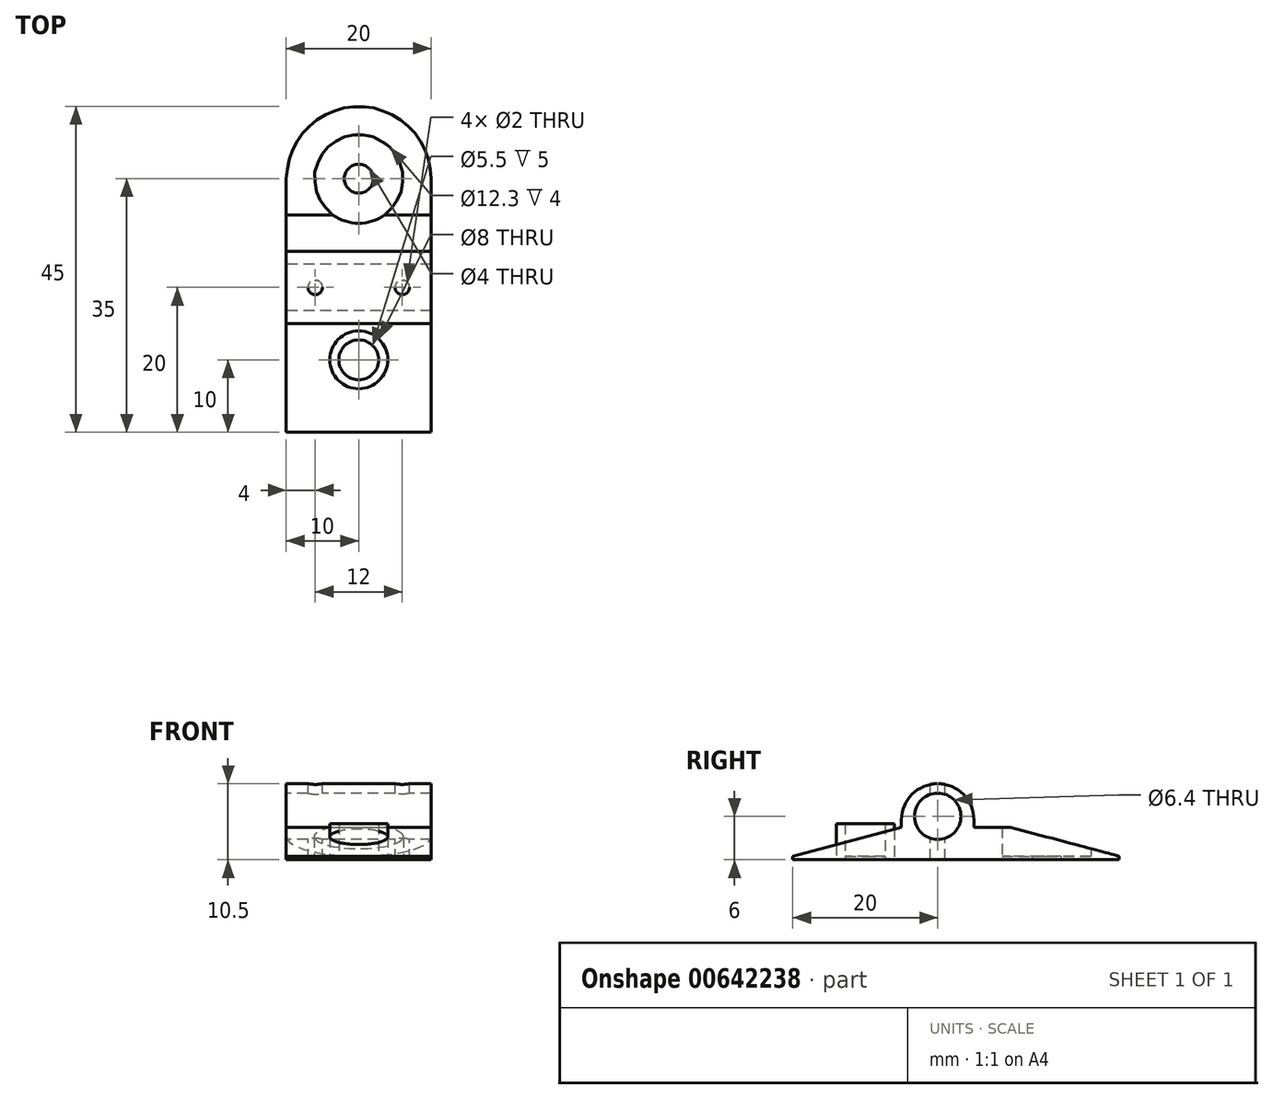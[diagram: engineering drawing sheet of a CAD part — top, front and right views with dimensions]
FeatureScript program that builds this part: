
annotation { "Feature Type Name" : "Feature", "Feature Type Description" : "" }
export const myFeature = defineFeature(function(context is Context, id is Id, definition is map)
    precondition{}
    {
        {
            var Q0;
            Q0=qCreatedBy(makeId("Top.planeOp"),FACE);
            var sketch = newSketch(context, id + "F0", { "sketchPlane" : qUnion([Q0])});
            skLineSegment(sketch, "E0.bottom", {"start": v(0, 0) * mm, "end": v(20, 0) * mm});
            skLineSegment(sketch, "E0.top", {"start": v(0, 45) * mm, "end": v(20, 45) * mm});
            skLineSegment(sketch, "E0.left", {"start": v(0, 0) * mm, "end": v(0, 45) * mm});
            skLineSegment(sketch, "E0.right", {"start": v(20, 0) * mm, "end": v(20, 45) * mm});
            skCircle(sketch, "E1", {"center": v(10, 35) * mm, "radius": 6.15 * mm});
            skCircle(sketch, "E2", {"center": v(10, 10) * mm, "radius": 2.75 * mm});
            skCircle(sketch, "E3", {"center": v(10, 35) * mm, "radius": 2 * mm});
            skCircle(sketch, "E4", {"center": v(10, 10) * mm, "radius": 4 * mm});
            skSolve(sketch);
        }
        {
            var Q0;
            Q0=makeQuery(id+"F0.imprint","IMPRINT",FACE,{"disambiguationData":[TD([[makeQuery(id+"F0.imprint","IMPRINT",EDGE,{"derivedFrom":sQuery(id+"F0.wireOp",EDGE,"E0.bottom")}),1.0]])]});
            extrude(context, id + "F1", {"entities" : qUnion([Q0]), "depth" : 4 * mm, "offsetDistance" : 25 * mm});
        }
        {
            var Q0;
            Q0=makeQuery(id+"F1.opExtrude","CAP_FACE",FACE,{"disambiguationData":[OSD([sQuery(id+"F0.wireOp",EDGE,"E0.bottom"),sQuery(id+"F0.wireOp",EDGE,"E0.top"),sQuery(id+"F0.wireOp",EDGE,"E0.left"),sQuery(id+"F0.wireOp",EDGE,"E0.right"),sQuery(id+"F0.wireOp",EDGE,"E1")])],"isStart":false});
            var Q1;
            Q1=makeQuery(id+"F0.imprint","IMPRINT",FACE,{"disambiguationData":[TD([[makeQuery(id+"F0.imprint","IMPRINT",EDGE,{"derivedFrom":sQuery(id+"F0.wireOp",EDGE,"E1")}),1.0]])]});
            var Q2;
            Q2=makeQuery(id+"F0.imprint","IMPRINT",FACE,{"disambiguationData":[TD([[makeQuery(id+"F0.imprint","IMPRINT",EDGE,{"derivedFrom":sQuery(id+"F0.wireOp",EDGE,"E2")}),1.0]])]});
            extrude(context, id + "F2", {"entities" : qUnion([Q0, Q1, Q2]), "operationType" : NewBodyOperationType.ADD, "depth" : 0.5 * mm, "offsetDistance" : 25 * mm});
        }
        {
            var Q0;
            Q0=makeQuery(id+"F2.opExtrude","CAP_FACE",FACE,{"disambiguationData":[OSD([sQuery(id+"F0.wireOp",EDGE,"E0.bottom"),sQuery(id+"F0.wireOp",EDGE,"E0.top"),sQuery(id+"F0.wireOp",EDGE,"E0.left"),sQuery(id+"F0.wireOp",EDGE,"E0.right"),sQuery(id+"F0.wireOp",EDGE,"E1")])],"isStart":false});
            var sketch = newSketch(context, id + "F3", { "sketchPlane" : qUnion([Q0])});
            skLineSegment(sketch, "E5.bottom", {"start": v(0, 15) * mm, "end": v(20, 15) * mm});
            skLineSegment(sketch, "E5.top", {"start": v(0, 25) * mm, "end": v(20, 25) * mm});
            skLineSegment(sketch, "E5.left", {"start": v(0, 15) * mm, "end": v(0, 25) * mm});
            skLineSegment(sketch, "E5.right", {"start": v(20, 15) * mm, "end": v(20, 25) * mm});
            skSolve(sketch);
        }
        {
            var Q0;
            Q0=makeQuery(id+"F2.opExtrude","CAP_EDGE",EDGE,{"disambiguationData":[OSD([sQuery(id+"F0.wireOp",EDGE,"E0.bottom")])],"isStart":false});
            chamfer(context, id + "F4", {"entities" : qUnion([Q0]), "chamferType" : ChamferType.TWO_OFFSETS, "width1" : 15 * mm, "oppositeDirection" : false, "width2" : 4 * mm, "tangentPropagation" : true});
        }
        {
            var Q0;
            Q0=makeQuery(id+"F0.imprint","IMPRINT",FACE,{"disambiguationData":[TD([[makeQuery(id+"F0.imprint","IMPRINT",EDGE,{"derivedFrom":sQuery(id+"F0.wireOp",EDGE,"E2")}),-1.0]])]});
            extrude(context, id + "F5", {"entities" : qUnion([Q0]), "depth" : 5 * mm, "offsetDistance" : 25 * mm});
        }
        {
            var Q0;
            Q0=makeQuery(id+"F3.imprint","IMPRINT",FACE,{"disambiguationData":[TD([[makeQuery(id+"F3.imprint","IMPRINT",EDGE,{"derivedFrom":sQuery(id+"F3.wireOp",EDGE,"E5.bottom")}),1.0]])]});
            extrude(context, id + "F6", {"entities" : qUnion([Q0]), "operationType" : NewBodyOperationType.ADD, "depth" : 6 * mm, "offsetDistance" : 25 * mm});
        }
        {
            var Q0;
            {var subQ0=sQuery(id+"F0.wireOp",EDGE,"E0.left");Q0=makeQuery(id+"F6.boolean.opBoolean","MERGE",FACE,{"derivedFrom":[makeQuery(id+"F2.boolean.opBoolean","MERGE",FACE,{"derivedFrom":[makeQuery(id+"F1.opExtrude","SWEPT_FACE",FACE,{"disambiguationData":[OSD([subQ0])]}),makeQuery(id+"F2.opExtrude","SWEPT_FACE",FACE,{"disambiguationData":[OSD([subQ0])]})]}),makeQuery(id+"F6.opExtrude","SWEPT_FACE",FACE,{"disambiguationData":[OSD([sQuery(id+"F3.wireOp",EDGE,"E5.left")])]})]});}
            var sketch = newSketch(context, id + "F7", { "sketchPlane" : qUnion([Q0])});
            skCircle(sketch, "E6", {"center": v(-20, 6) * mm, "radius": 3.2 * mm});
            skSolve(sketch);
        }
        {
            var Q0;
            Q0=makeQuery(id+"F7.imprint","IMPRINT",FACE,{"disambiguationData":[TD([[makeQuery(id+"F7.imprint","IMPRINT",EDGE,{"derivedFrom":sQuery(id+"F7.wireOp",EDGE,"E6")}),1.0]])]});
            extrude(context, id + "F8", {"entities" : qUnion([Q0]), "operationType" : NewBodyOperationType.REMOVE, "oppositeDirection" : true, "depth" : 25 * mm, "offsetDistance" : 25 * mm});
        }
        {
            var Q0;
            Q0=makeQuery(id+"F2.opExtrude","CAP_EDGE",EDGE,{"disambiguationData":[OSD([sQuery(id+"F0.wireOp",EDGE,"E0.top")])],"isStart":false});
            chamfer(context, id + "F9", {"entities" : qUnion([Q0]), "chamferType" : ChamferType.TWO_OFFSETS, "width1" : 4 * mm, "oppositeDirection" : false, "width2" : 15 * mm, "tangentPropagation" : true});
        }
        {
            var Q0;
            {var subQ0=sQuery(id+"F0.wireOp",EDGE,"E0.left");var subQ1=sQuery(id+"F0.wireOp",EDGE,"E0.top");Q0=makeQuery(id+"F2.boolean.opBoolean","MERGE",EDGE,{"derivedFrom":[makeQuery(id+"F1.opExtrude","SWEPT_EDGE",EDGE,{"disambiguationData":[OSD([subQ1,subQ0])]}),makeQuery(id+"F2.opExtrude","SWEPT_EDGE",EDGE,{"disambiguationData":[OSD([subQ1,subQ0])]})]});}
            var Q1;
            {var subQ0=sQuery(id+"F0.wireOp",EDGE,"E0.right");var subQ1=sQuery(id+"F0.wireOp",EDGE,"E0.top");Q1=makeQuery(id+"F2.boolean.opBoolean","MERGE",EDGE,{"derivedFrom":[makeQuery(id+"F1.opExtrude","SWEPT_EDGE",EDGE,{"disambiguationData":[OSD([subQ1,subQ0])]}),makeQuery(id+"F2.opExtrude","SWEPT_EDGE",EDGE,{"disambiguationData":[OSD([subQ1,subQ0])]})]});}
            fillet(context, id + "F10", {"entities" : qUnion([Q0, Q1]), "radius" : 10 * mm, "tangentPropagation" : true, "allowEdgeOverflow" : false});
        }
        {
            var Q0;
            Q0=makeQuery(id+"F6.opExtrude","CAP_FACE",FACE,{"disambiguationData":[OSD([sQuery(id+"F3.wireOp",EDGE,"E5.bottom"),sQuery(id+"F3.wireOp",EDGE,"E5.top"),sQuery(id+"F3.wireOp",EDGE,"E5.left"),sQuery(id+"F3.wireOp",EDGE,"E5.right")])],"isStart":false});
            var sketch = newSketch(context, id + "F11", { "sketchPlane" : qUnion([Q0])});
            skCircle(sketch, "E7", {"center": v(16, 20) * mm, "radius": 1 * mm});
            skCircle(sketch, "E8", {"center": v(4, 20) * mm, "radius": 1 * mm});
            skSolve(sketch);
        }
        {
            var Q0;
            Q0=makeQuery(id+"F11.imprint","IMPRINT",FACE,{"disambiguationData":[TD([[makeQuery(id+"F11.imprint","IMPRINT",EDGE,{"derivedFrom":sQuery(id+"F11.wireOp",EDGE,"E8")}),1.0]])]});
            var Q1;
            Q1=makeQuery(id+"F11.imprint","IMPRINT",FACE,{"disambiguationData":[TD([[makeQuery(id+"F11.imprint","IMPRINT",EDGE,{"derivedFrom":sQuery(id+"F11.wireOp",EDGE,"E7")}),1.0]])]});
            extrude(context, id + "F12", {"entities" : qUnion([Q0, Q1]), "operationType" : NewBodyOperationType.REMOVE, "oppositeDirection" : true, "depth" : 25 * mm, "offsetDistance" : 25 * mm});
        }
        {
            var Q0;
            Q0=makeQuery(id+"F6.opExtrude","CAP_EDGE",EDGE,{"disambiguationData":[OSD([sQuery(id+"F3.wireOp",EDGE,"E5.top")])],"isStart":false});
            var Q1;
            Q1=makeQuery(id+"F6.opExtrude","CAP_EDGE",EDGE,{"disambiguationData":[OSD([sQuery(id+"F3.wireOp",EDGE,"E5.bottom")])],"isStart":false});
            fillet(context, id + "F13", {"entities" : qUnion([Q0, Q1]), "radius" : 5 * mm, "tangentPropagation" : true, "allowEdgeOverflow" : false});
        }
    });
